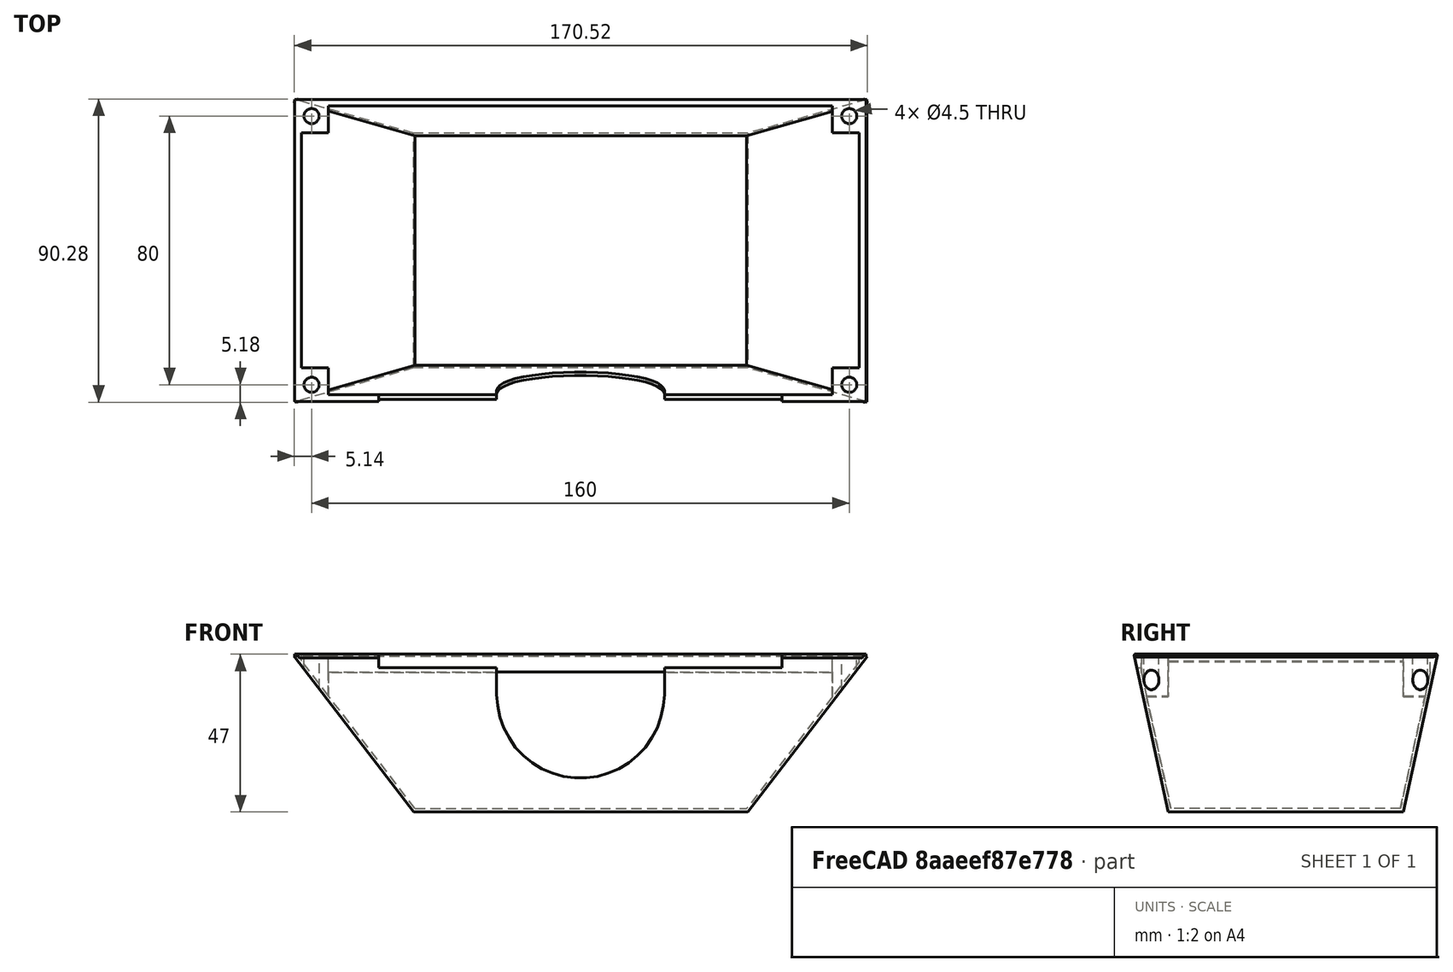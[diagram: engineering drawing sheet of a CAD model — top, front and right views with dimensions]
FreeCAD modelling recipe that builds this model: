
FCSTD DOCUMENT  (FreeCAD 0.16R)
Label: bierdisplay-gehäuse_v1.1
License: All rights reserved
LicenseURL: http://en.wikipedia.org/wiki/All_rights_reserved
objects: Part::Box×19, Part::Fuse×12, Part::Cut×11, Part::Cylinder×5
note: 47 computed .brp shape members not serialized (recipe doc carries the construction recipe); baked Part::Feature solids carry a one-line shape summary decoded from their .brp

FEATURE [Part::Box] Box002  label="Cube002"
  Height = 1
  Length = 58
  Placement = pos=(5,0,46) rot=(0,1,0;0.916298rad)
  Width = 100
FEATURE [Part::Box] Box003  label="Cube003"
  Height = 1
  Length = 58
  Placement = pos=(140,0,0.1) rot=(0,-1,0;0.916298rad)
  Width = 100
FEATURE [Part::Box] Box004  label="Cube004"
  Height = 47
  Length = 180
  Placement = pos=(1,15,0) rot=(1,0,0;0.214675rad)
  Width = 1
FEATURE [Part::Box] Box005  label="Cube005"
  Height = 47
  Length = 180
  Placement = pos=(1,84,0.4) rot=(-1,0,0;0.214675rad)
  Width = 1
FEATURE [Part::Box] Box007  label="Cube007"
  Height = 1
  Length = 100
  Placement = pos=(40,15,0) rot=(0,0,1;0rad)
  Width = 70
FEATURE [Part::Cylinder] Cylinder  label="Cylinder000"
  Angle = 360
  Height = 60
  Placement = pos=(10,10,0) rot=(0,0,1;0rad)
  Radius = 2.25
FEATURE [Part::Cylinder] Cylinder001
  Angle = 360
  Height = 60
  Placement = pos=(170,10,0) rot=(0,0,1;0rad)
  Radius = 2.25
FEATURE [Part::Cylinder] Cylinder002
  Angle = 360
  Height = 60
  Placement = pos=(10,90,0) rot=(0,0,1;0rad)
  Radius = 2.25
FEATURE [Part::Cylinder] Cylinder003
  Angle = 360
  Height = 60
  Placement = pos=(170,90,0) rot=(0,0,1;0rad)
  Radius = 2.25
FEATURE [Part::Box] Box  label="Cube"
  Height = 13
  Length = 10
  Placement = pos=(5,5,34) rot=(0,0,1;0rad)
  Width = 10
FEATURE [Part::Box] Box008  label="Cube008"
  Height = 13
  Length = 10
  Placement = pos=(165,5,34) rot=(0,0,1;0rad)
  Width = 10
FEATURE [Part::Box] Box009  label="Cube009"
  Height = 13
  Length = 10
  Placement = pos=(165,85,34) rot=(0,0,1;0rad)
  Width = 10
FEATURE [Part::Box] Box010  label="Cube010"
  Height = 13
  Length = 10
  Placement = pos=(5,85,34) rot=(0,0,1;0rad)
  Width = 10
FEATURE [Part::Box] Box011  label="Cube011"
  Height = 2.5
  Length = 2
  Placement = pos=(5,5,44.5) rot=(0,0,1;0rad)
  Width = 80
FEATURE [Part::Box] Box012  label="Cube012"
  Height = 2.5
  Length = 2
  Placement = pos=(173,5,44.5) rot=(0,0,1;0rad)
  Width = 80
FEATURE [Part::Box] Box013  label="Cube013"
  Height = 7
  Length = 170
  Placement = pos=(5,5,40) rot=(0,0,1;0rad)
  Width = 2
FEATURE [Part::Box] Box014  label="Cube014"
  Height = 7
  Length = 170
  Placement = pos=(5,93,40) rot=(0,0,1;0rad)
  Width = 2
FEATURE [Part::Box] Box015  label="Cube015"
  Height = 50
  Length = 70
  Placement = pos=(176,0,-35) rot=(0,-1,0;0.916298rad)
  Width = 100
FEATURE [Part::Box] Box016  label="Cube016"
  Height = 50
  Length = 70
  Placement = pos=(-39.5,0,22) rot=(0,1,0;0.916298rad)
  Width = 100
FEATURE [Part::Box] Box017  label="Cube017"
  Height = 60
  Length = 180
  Placement = pos=(1,-32.9,-15) rot=(1,0,0;0.214675rad)
  Width = 50
FEATURE [Part::Box] Box018  label="Cube018"
  Height = 60
  Length = 180
  Placement = pos=(1,84,-4.2) rot=(-1,0,0;0.214675rad)
  Width = 50
FEATURE [Part::Fuse] Fusion
  Base = -> Box002
  Tool = -> Box003
FEATURE [Part::Fuse] Fusion001
  Base = -> Box004
  Tool = -> Box005
FEATURE [Part::Fuse] Fusion002
  Base = -> Fusion
  Tool = -> Fusion001
FEATURE [Part::Fuse] Fusion003
  Base = -> Fusion002
  Tool = -> Box
FEATURE [Part::Fuse] Fusion004
  Base = -> Fusion003
  Tool = -> Box008
FEATURE [Part::Fuse] Fusion005
  Base = -> Fusion004
  Tool = -> Box009
FEATURE [Part::Fuse] Fusion006
  Base = -> Fusion005
  Tool = -> Box010
FEATURE [Part::Fuse] Fusion007
  Base = -> Fusion006
  Tool = -> Box011
FEATURE [Part::Fuse] Fusion008
  Base = -> Fusion007
  Tool = -> Box012
FEATURE [Part::Fuse] Fusion009
  Base = -> Fusion008
  Tool = -> Box013
FEATURE [Part::Fuse] Fusion010
  Base = -> Fusion009
  Tool = -> Box014
FEATURE [Part::Fuse] Fusion011
  Base = -> Fusion010
  Tool = -> Box007
FEATURE [Part::Cut] Cut
  Base = -> Fusion011
  Tool = -> Box015
FEATURE [Part::Cut] Cut001
  Base = -> Cut
  Tool = -> Box016
FEATURE [Part::Cut] Cut002
  Base = -> Cut001
  Tool = -> Box017
FEATURE [Part::Cut] Cut003
  Base = -> Cut002
  Tool = -> Box018
FEATURE [Part::Cut] Cut004
  Base = -> Cut003
  Tool = -> Cylinder
FEATURE [Part::Cut] Cut005
  Base = -> Cut004
  Tool = -> Cylinder001
FEATURE [Part::Cut] Cut006
  Base = -> Cut005
  Tool = -> Cylinder002
FEATURE [Part::Cut] Cut007
  Base = -> Cut006
  Tool = -> Cylinder003
FEATURE [Part::Box] Box019  label="Cube019"
  Height = 10
  Length = 120
  Placement = pos=(30,0,43) rot=(0,0,1;0rad)
  Width = 10
FEATURE [Part::Cut] Cut008
  Base = -> Cut007
  Tool = -> Box019
FEATURE [Part::Cylinder] Cylinder004  label="Cylinder"
  Angle = 360
  Height = 20
  Placement = pos=(90,20,35) rot=(1,0,0;1.5708rad)
  Radius = 25
FEATURE [Part::Box] Box020  label="Cube020"
  Height = 25
  Length = 50
  Placement = pos=(65,0,35) rot=(0,0,1;0rad)
  Width = 20
FEATURE [Part::Cut] Cut009
  Base = -> Cut008
  Tool = -> Cylinder004
FEATURE [Part::Cut] Cut010
  Base = -> Cut009
  Tool = -> Box020
